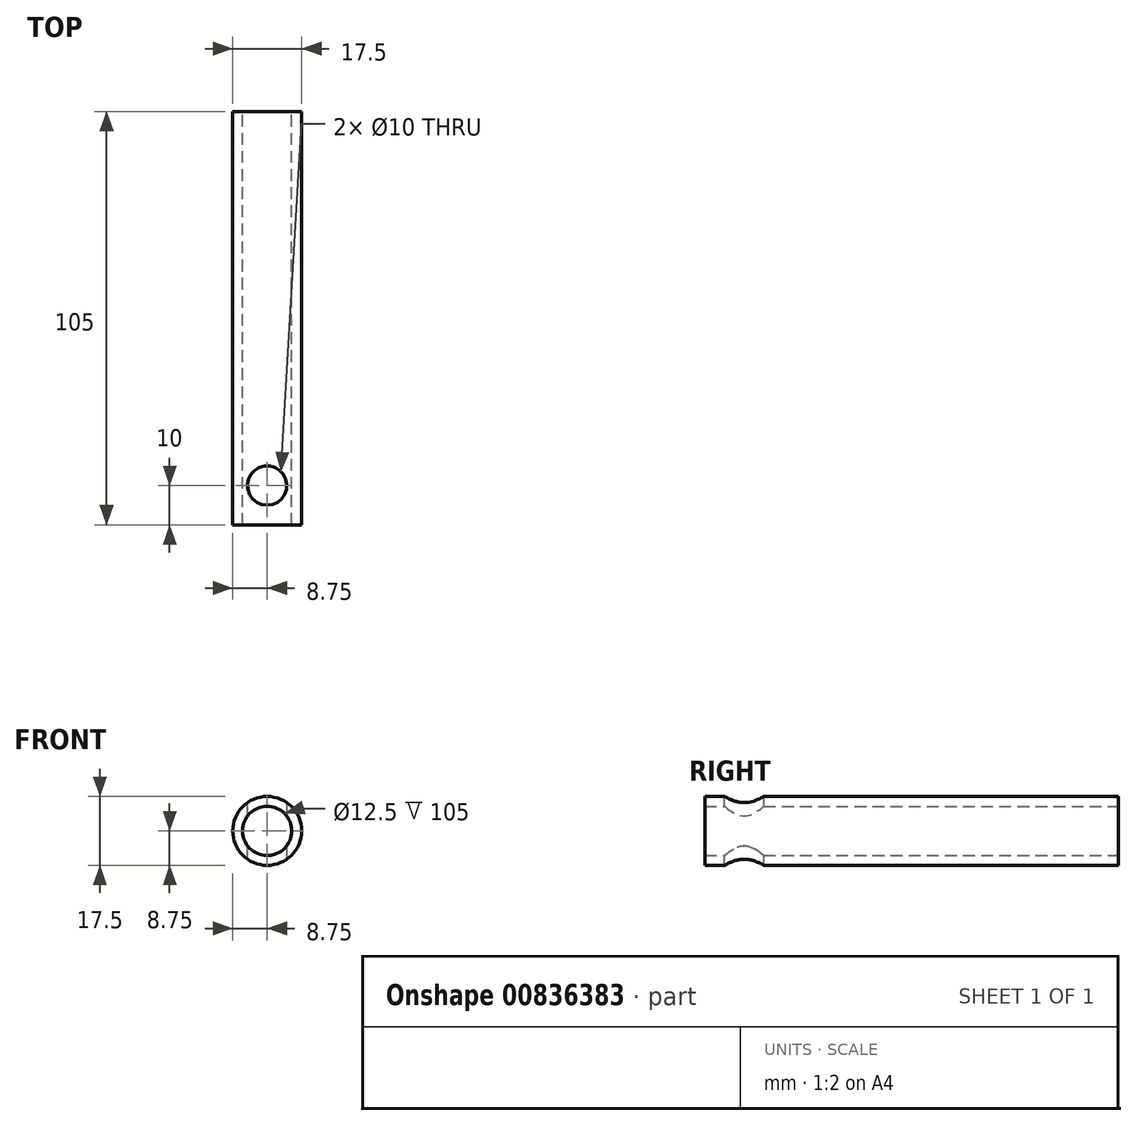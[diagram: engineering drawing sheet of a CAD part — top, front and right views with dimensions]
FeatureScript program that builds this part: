
annotation { "Feature Type Name" : "Feature", "Feature Type Description" : "" }
export const myFeature = defineFeature(function(context is Context, id is Id, definition is map)
    precondition{}
    {
        {
            var Q0;
            Q0=qCreatedBy(makeId("Front.planeOp"),FACE);
            var sketch = newSketch(context, id + "F0", { "sketchPlane" : qUnion([Q0])});
            skCircle(sketch, "E0", {"center": v(0, 0) * mm, "radius": 6.25 * mm});
            skCircle(sketch, "E1", {"center": v(0, 0) * mm, "radius": 8.75 * mm});
            skSolve(sketch);
        }
        {
            var Q0;
            Q0=makeQuery(id+"F0.imprint","IMPRINT",FACE,{"disambiguationData":[TD([[makeQuery(id+"F0.imprint","IMPRINT",EDGE,{"derivedFrom":sQuery(id+"F0.wireOp",EDGE,"E0")}),-1.0]])]});
            extrude(context, id + "F1", {"entities" : qUnion([Q0]), "depth" : 105 * mm, "offsetDistance" : 25 * mm});
        }
        {
            var Q0;
            Q0=qCreatedBy(makeId("Top.planeOp"),FACE);
            var sketch = newSketch(context, id + "F2", { "sketchPlane" : qUnion([Q0])});
            skLineSegment(sketch, "E2", {"start": v(0, 0) * mm, "end": v(0, -95) * mm, "construction": true});
            skCircle(sketch, "E3", {"center": v(0, -95) * mm, "radius": 5 * mm});
            skSolve(sketch);
        }
        {
            var Q0;
            Q0=makeQuery(id+"F2.imprint","IMPRINT",FACE,{"disambiguationData":[TD([[makeQuery(id+"F2.imprint","IMPRINT",EDGE,{"derivedFrom":sQuery(id+"F2.wireOp",EDGE,"E3")}),1.0]])]});
            extrude(context, id + "F3", {"entities" : qUnion([Q0]), "operationType" : NewBodyOperationType.REMOVE, "endBound" : BoundingType.SYMMETRIC, "oppositeDirection" : true, "depth" : 67.2 * mm, "offsetDistance" : 25 * mm});
        }
    });
